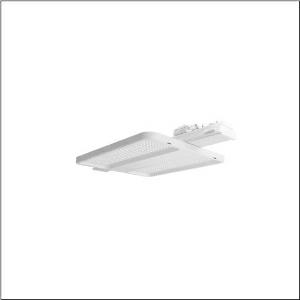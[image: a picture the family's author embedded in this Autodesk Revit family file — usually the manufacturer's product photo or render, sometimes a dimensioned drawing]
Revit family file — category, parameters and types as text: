
# Revit family: highbay_21_fur_licross_r__tragschiene_midi_52hn11da4fla_c4fb
name_source: partatom
category: Lighting Fixtures
units: mm (PartAtom-declared; Revit-internal decimal feet)

## family parameters
Cut with Voids When Loaded = No
Host = Face
Light Source = No
Part Type = Normal
Room Calculation Point = No
Round Connector Dimension = Use Diameter
Shared = No

## types (1)
- --- (1 x LED, 14000 lm, 72.1 W, 4000K)
    Apparent Load = 72 VA
    CIE Flux Codes = 89 97 99 100 100
    Color Rendering = 80
    Color Temperature = 4000K
    Default Elevation = 1800 mm
    Description = Highbay 21 for Licross® trunking rail midi, high bay luminaire, primary light control with lens, of PMMA, primary optical cover: cover, of PMMA, light emission: direct distribution, primary light characteristic: symmetric, LED, rated luminous flux: 14.000lm, luminous efficacy: 194lm/W, light colour: 840, colour temperature: 4000K, control gear: DALI 2, with plug, 5-pole, with phase selection, mains connection: 230..240V, AC, 50/60Hz, rated input power: 72.1W, housing frame, of high-performance plastic PA6, matt traffic white (RAL 9016), length: 750mm, width: 442mm, height: 71mm, lever catch, fixing on rail side, of steel, galvanised, white, blank cover, of PC/ABS, traffic white (RAL 9016), protection rating (complete): IP64, insulation class (complete): insulation class I (protective earthing), certification: CE, ENEC, VDE, UKCA, protection symbol: D, impact resistance: IK07, permissible operating ambient temperature: -40..+55°C, LABS conformity tested according to VDMA 24364:2018-05, corresponds to IFS (International Featured Standards) requirements for safety and quality in the food industry, packaging unit: 1 piece
    Height = 72 mm  [stored 0.23622 ft]
    Lamp = 1 x LED
    Lamp Light Flux = 14000 lm
    Lamp Power = 72.1 W
    Lamp count = 1
    Length = 474 mm
    Luminous efficacy = 194 lm/W
    Manufacturer = Siteco
    ModVariant = No
    Model = 52HN11DA4FLA
    Mounting Place = Ceiling
    Mounting Type = Pendant
    Number of Poles = 1
    OnlyDefault = Yes
    Power Factor = 1
    Product Name = Highbay 21 für Licross® Tragschiene midi
    Product group = high bay luminaire
    ProductGroupID = 901
    Protection Class = Protection class I
    Protection Degree = IP 64
    RLX_Detail_Level = 1
    RLX_Emergency_Light_Flux = 0 lm
    RLX_Emergency_Type = 0
    RLX_Emergency_Type_DB = No
    RlxData = <blob elided: 17689 chars, md5=b982bd1e>
    Socket = socket
    Standby Power = 0 W
    System Light Flux = 14000 lm
    System Power = 72 W
    Type Comments = factory setting: luminous flux: 100 % | dim-lin: 254 | 334 mA
    Type Image = l_1363258.jpg
    URL = http://relux.com
    VarID = @adj_000127
    Voltage = 0 V
    Weight = 0.00 kg
    Width = 442 mm

note: [stored X ft] marks values corroborated as IEEE doubles in the binary element streams (Revit-internal decimal feet)

## geometry (parser evidence)
native form markers: Blend x4, Sweep x10
no freeform markers — native parametric forms only
